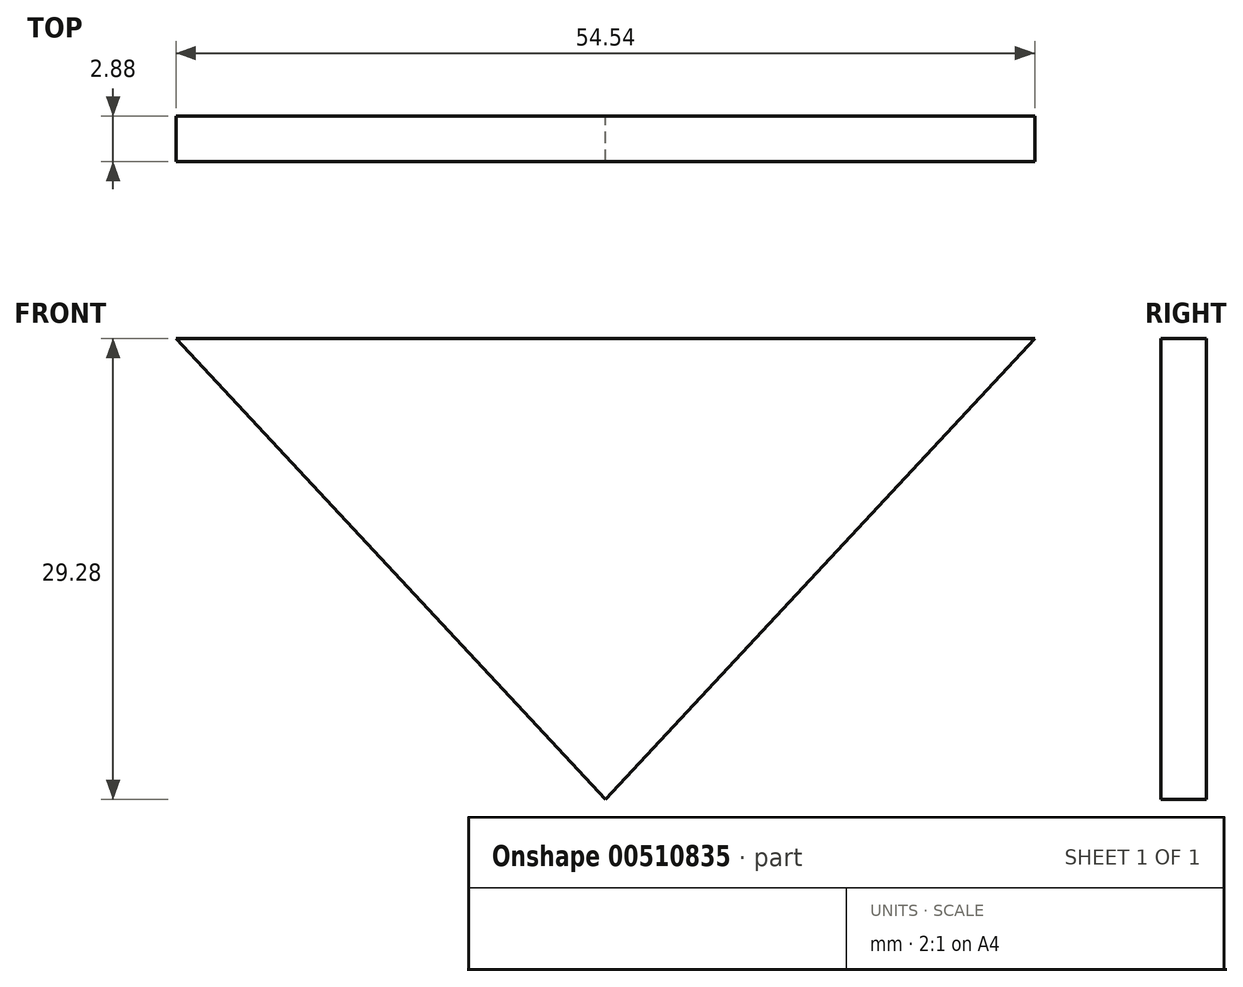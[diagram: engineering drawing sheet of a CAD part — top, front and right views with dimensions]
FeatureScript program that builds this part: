
annotation { "Feature Type Name" : "Feature", "Feature Type Description" : "" }
export const myFeature = defineFeature(function(context is Context, id is Id, definition is map)
    precondition{}
    {
        {
            var Q0;
            Q0=qCreatedBy(makeId("Front.planeOp"),FACE);
            var sketch = newSketch(context, id + "F0", { "sketchPlane" : qUnion([Q0])});
            skLineSegment(sketch, "E0.bottom", {"start": v(-27.27, 14.64) * mm, "end": v(27.27, 14.64) * mm});
            skLineSegment(sketch, "E0.top", {"start": v(-27.27, -14.64) * mm, "end": v(27.27, -14.64) * mm});
            skLineSegment(sketch, "E0.left", {"start": v(-27.27, 14.64) * mm, "end": v(-27.27, -14.64) * mm});
            skLineSegment(sketch, "E0.right", {"start": v(27.27, 14.64) * mm, "end": v(27.27, -14.64) * mm});
            skPoint(sketch, "E0.middle", {"position": v(0, 0) * mm});
            skLineSegment(sketch, "E1", {"start": v(-27.27, 14.64) * mm, "end": v(0, -14.64) * mm});
            skLineSegment(sketch, "E2", {"start": v(0, -14.64) * mm, "end": v(27.27, 14.64) * mm});
            skLineSegment(sketch, "E3", {"start": v(0, 14.64) * mm, "end": v(0, -14.64) * mm});
            skSolve(sketch);
        }
        {
            var Q0;
            {var subQ0=sQuery(id+"F0.wireOp",EDGE,"E1");Q0=makeQuery(id+"F0.imprint","IMPRINT",FACE,{"disambiguationData":[TD([[makeQuery(id+"F0.imprint","IMPRINT",EDGE,{"derivedFrom":subQ0}),1.0]])]});}
            var Q1;
            {var subQ0=sQuery(id+"F0.wireOp",EDGE,"E2");Q1=makeQuery(id+"F0.imprint","IMPRINT",FACE,{"disambiguationData":[TD([[makeQuery(id+"F0.imprint","IMPRINT",EDGE,{"derivedFrom":subQ0}),1.0]])]});}
            extrude(context, id + "F1", {"entities" : qUnion([Q0, Q1]), "endBound" : BoundingType.SYMMETRIC, "depth" : 2.88 * mm});
        }
    });
